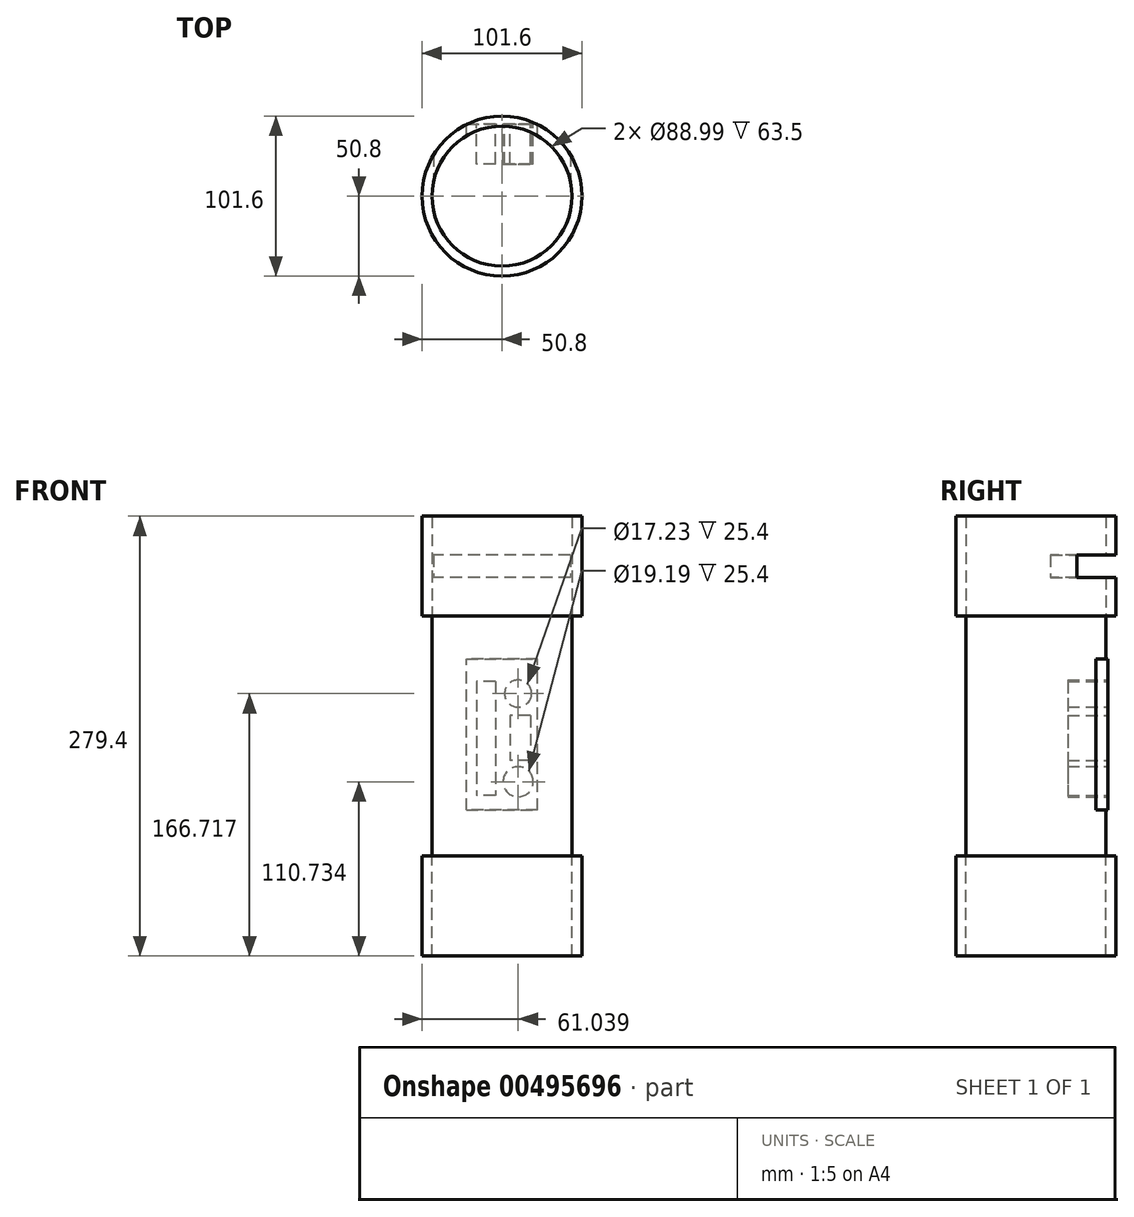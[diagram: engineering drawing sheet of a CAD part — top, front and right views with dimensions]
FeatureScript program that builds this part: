
annotation { "Feature Type Name" : "Feature", "Feature Type Description" : "" }
export const myFeature = defineFeature(function(context is Context, id is Id, definition is map)
    precondition{}
    {
        {
            var Q0;
            Q0=qCreatedBy(makeId("Top.planeOp"),FACE);
            var sketch = newSketch(context, id + "F0", { "sketchPlane" : qUnion([Q0])});
            skCircle(sketch, "E0", {"center": v(0, 0) * mm, "radius": 44.5 * mm});
            skSolve(sketch);
        }
        {
            var Q0;
            Q0 = qSketchRegion(id + "F0", true);
            extrude(context, id + "F1", {"entities" : qUnion([Q0]), "depth" : 152.4 * mm});
        }
        {
            var Q0;
            Q0=makeQuery(id+"F1.opExtrude","CAP_FACE",FACE,{"disambiguationData":[OSD([sQuery(id+"F0.wireOp",EDGE,"E0")])],"isStart":false});
            var sketch = newSketch(context, id + "F2", { "sketchPlane" : qUnion([Q0])});
            skCircle(sketch, "E1", {"center": v(0, 0) * mm, "radius": 50.8 * mm});
            skSolve(sketch);
        }
        {
            var Q0;
            Q0=makeQuery(id+"F2.imprint","IMPRINT",FACE,{"disambiguationData":[TD([[makeQuery(id+"F2.imprint","IMPRINT",EDGE,{"derivedFrom":sQuery(id+"F2.wireOp",EDGE,"E1")}),1.0]])]});
            extrude(context, id + "F3", {"entities" : qUnion([Q0]), "depth" : 63.5 * mm});
        }
        {
            var Q0;
            Q0=makeQuery(id+"F1.opExtrude","CAP_FACE",FACE,{"disambiguationData":[OSD([sQuery(id+"F0.wireOp",EDGE,"E0")])],"isStart":true});
            var sketch = newSketch(context, id + "F4", { "sketchPlane" : qUnion([Q0])});
            skCircle(sketch, "E2", {"center": v(0, 0) * mm, "radius": 50.8 * mm});
            skSolve(sketch);
        }
        {
            var Q0;
            Q0=makeQuery(id+"F4.imprint","IMPRINT",FACE,{"disambiguationData":[TD([[makeQuery(id+"F4.imprint","IMPRINT",EDGE,{"derivedFrom":sQuery(id+"F4.wireOp",EDGE,"E2")}),1.0]])]});
            extrude(context, id + "F5", {"entities" : qUnion([Q0]), "depth" : 63.5 * mm});
        }
        {
            var Q0;
            Q0=qCreatedBy(makeId("Front.planeOp"),FACE);
            var sketch = newSketch(context, id + "F6", { "sketchPlane" : qUnion([Q0])});
            skLineSegment(sketch, "E3.bottom", {"start": v(43.5, 176.98) * mm, "end": v(-43.5, 176.98) * mm});
            skLineSegment(sketch, "E3.top", {"start": v(43.5, 191.1) * mm, "end": v(-43.5, 191.1) * mm});
            skLineSegment(sketch, "E3.left", {"start": v(43.5, 176.98) * mm, "end": v(43.5, 191.1) * mm});
            skLineSegment(sketch, "E3.right", {"start": v(-43.5, 176.98) * mm, "end": v(-43.5, 191.1) * mm});
            skPoint(sketch, "E3.middle", {"position": v(0, 184.04) * mm});
            skSolve(sketch);
        }
        {
            var Q0;
            Q0 = qSketchRegion(id + "F6", true);
            extrude(context, id + "F7", {"entities" : qUnion([Q0]), "operationType" : NewBodyOperationType.REMOVE, "oppositeDirection" : true, "depth" : 66.3 * mm});
        }
        {
            var Q0;
            Q0=qCreatedBy(makeId("Front.planeOp"),FACE);
            cPlane(context, id + "F8", {"entities" : qUnion([Q0]), "cplaneType" : CPlaneType.OFFSET, "offset" : 45.72 * mm, "oppositeDirection" : true, "width" : 152.4 * mm, "height" : 152.4 * mm});
        }
        {
            var Q0;
            Q0=qCreatedBy(id+"F8.planeOp",FACE);
            var sketch = newSketch(context, id + "F9", { "sketchPlane" : qUnion([Q0])});
            skLineSegment(sketch, "E4.bottom", {"start": v(-22.65, 29.29) * mm, "end": v(22.65, 29.29) * mm});
            skLineSegment(sketch, "E4.top", {"start": v(-22.65, 125.19) * mm, "end": v(22.65, 125.19) * mm});
            skLineSegment(sketch, "E4.left", {"start": v(-22.65, 29.29) * mm, "end": v(-22.65, 125.19) * mm});
            skLineSegment(sketch, "E4.right", {"start": v(22.65, 29.29) * mm, "end": v(22.65, 125.19) * mm});
            skPoint(sketch, "E4.middle", {"position": v(0, 77.24) * mm});
            skSolve(sketch);
        }
        {
            var Q0;
            Q0 = qSketchRegion(id + "F9", true);
            extrude(context, id + "F10", {"entities" : qUnion([Q0]), "operationType" : NewBodyOperationType.ADD, "depth" : 25.4 * mm});
        }
        {
            var Q0;
            Q0=makeQuery(id+"F10.opExtrude","CAP_FACE",FACE,{"disambiguationData":[OSD([sQuery(id+"F9.wireOp",EDGE,"E4.bottom"),sQuery(id+"F9.wireOp",EDGE,"E4.top"),sQuery(id+"F9.wireOp",EDGE,"E4.left"),sQuery(id+"F9.wireOp",EDGE,"E4.right")])],"isStart":true});
            var sketch = newSketch(context, id + "F11", { "sketchPlane" : qUnion([Q0])});
            skCircle(sketch, "E5", {"center": v(-10.24, 103.22) * mm, "radius": 8.61 * mm});
            skCircle(sketch, "E6", {"center": v(-10.24, 47.23) * mm, "radius": 9.6 * mm});
            skLineSegment(sketch, "E7.bottom", {"start": v(-18.24, 89.22) * mm, "end": v(-5.04, 89.22) * mm});
            skLineSegment(sketch, "E7.top", {"start": v(-18.24, 60.83) * mm, "end": v(-5.04, 60.83) * mm});
            skLineSegment(sketch, "E7.left", {"start": v(-18.24, 89.22) * mm, "end": v(-18.24, 60.83) * mm});
            skLineSegment(sketch, "E7.right", {"start": v(-5.04, 89.22) * mm, "end": v(-5.04, 60.83) * mm});
            skLineSegment(sketch, "E8.bottom", {"start": v(4.16, 110.81) * mm, "end": v(16.15, 110.81) * mm});
            skLineSegment(sketch, "E8.top", {"start": v(4.16, 38.44) * mm, "end": v(16.15, 38.44) * mm});
            skLineSegment(sketch, "E8.left", {"start": v(4.16, 110.81) * mm, "end": v(4.16, 38.44) * mm});
            skLineSegment(sketch, "E8.right", {"start": v(16.15, 110.81) * mm, "end": v(16.15, 38.44) * mm});
            skSolve(sketch);
        }
        {
            var Q0;
            Q0 = qSketchRegion(id + "F11", true);
            extrude(context, id + "F12", {"entities" : qUnion([Q0]), "operationType" : NewBodyOperationType.REMOVE, "oppositeDirection" : true, "depth" : 25.4 * mm, "offsetDistance" : 25.4 * mm});
        }
    });
